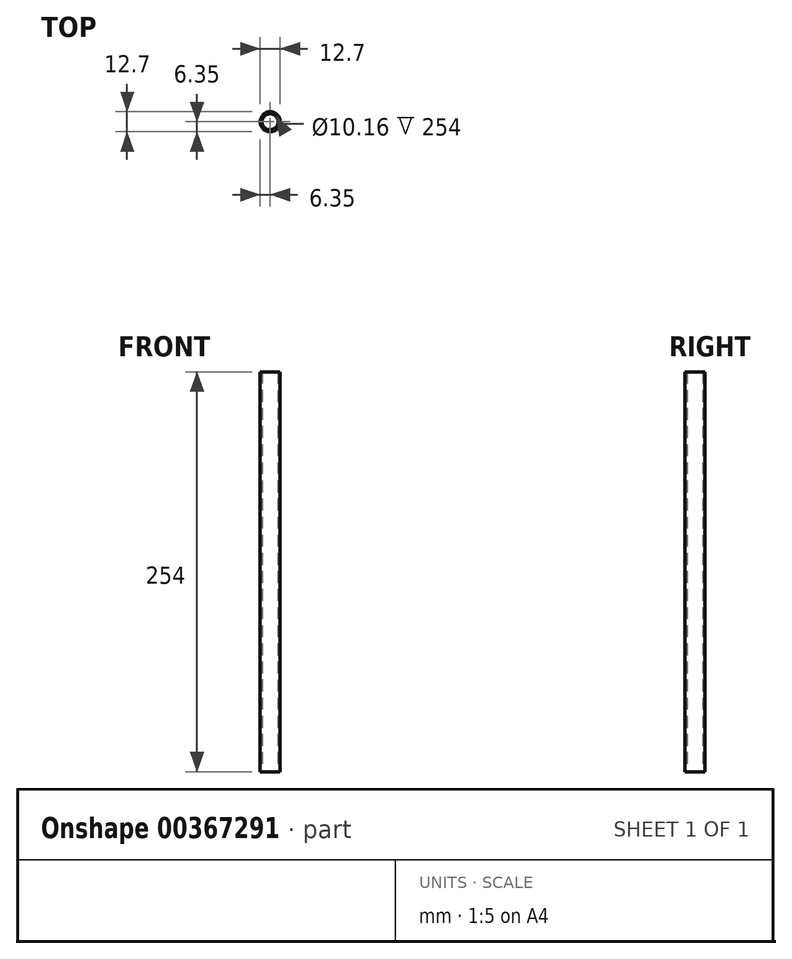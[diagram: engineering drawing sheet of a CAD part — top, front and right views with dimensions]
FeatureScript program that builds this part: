
annotation { "Feature Type Name" : "Feature", "Feature Type Description" : "" }
export const myFeature = defineFeature(function(context is Context, id is Id, definition is map)
    precondition{}
    {
        {
            var Q0;
            Q0=qCreatedBy(makeId("Top.planeOp"),FACE);
            var sketch = newSketch(context, id + "F0", { "sketchPlane" : qUnion([Q0])});
            skCircle(sketch, "E0", {"center": v(0, 0) * mm, "radius": 5.08 * mm});
            skCircle(sketch, "E1", {"center": v(0, 0) * mm, "radius": 6.35 * mm});
            skSolve(sketch);
        }
        {
            var Q0;
            Q0=qSketchRegion(id+"F0",true);
            extrude(context, id + "F1", {"entities" : qUnion([Q0]), "depth" : 254 * mm});
        }
    });
